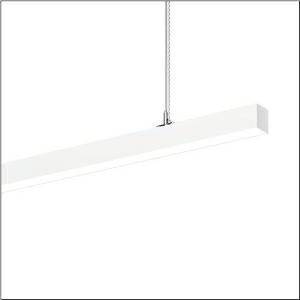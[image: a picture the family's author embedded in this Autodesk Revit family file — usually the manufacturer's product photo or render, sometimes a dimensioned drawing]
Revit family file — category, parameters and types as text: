
# Revit family: silica_r__21_51mx30tat4w_7b2a
name_source: partatom
category: Lighting Fixtures
units: mm (PartAtom-declared; Revit-internal decimal feet)

## family parameters
Cut with Voids When Loaded = No
Host = Face
Light Source = No
Part Type = Normal
Room Calculation Point = No
Round Connector Dimension = Use Diameter
Shared = No

## types (1)
- --- (1 x LED, 4120 lm, 33.8 W, 6500K)
    Apparent Load = 34 VA
    CIE Flux Codes = 47 79 96 58 100
    Color Rendering = 80
    Color Temperature = 6500K
    Default Elevation = 1800 mm
    Description = Silica® 21, office luminaire, primary optical cover: cover, of PMMA, opal, light emission: direct/indirect distribution, primary light characteristic: symmetric, installation type: suspended mounting, LED, rated luminous flux: 4.120lm, luminous efficacy: 116lm/W, light colour: 8tw, colour temperature: 2700..6500K, control gear: DALI DT8, with terminal, 3+2-pole, max. 2.5mm², mains connection: 220..240V, AC, 50/60Hz, rated input power: 35.5W, luminaire housing, of aluminium, traffic white (RAL 9016), length: 1.204mm, width: 53mm, height: 53mm, protection rating (complete): IP20, insulation class (complete): insulation class I (protective earthing), certification: CE, permissible operating ambient temperature: 0..+35°C, standard: EN 50419, packaging unit: 1 piece
    Height = 53 mm
    Lamp = 1 x LED
    Lamp Light Flux = 4120 lm
    Lamp Power = 33.8 W
    Lamp count = 1
    Length = 1204 mm
    Luminous efficacy = 122 lm/W
    Manufacturer = Siteco
    ModVariant = No
    Model = 51MX30TAT4W
    Mounting Place = Ceiling
    Mounting Type = Pendant
    Number of Poles = 1
    OnlyDefault = Yes
    Power Factor = 1
    Product Name = Silica® 21
    Product group = office luminaire | ceiling pendant
    ProductGroupID = 904
    Protection Class = Protection class I
    Protection Degree = IP 20
    RLX_Detail_Level = 1
    RLX_Emergency_Light_Flux = 0 lm
    RLX_Emergency_Type = 0
    RLX_Emergency_Type_DB = No
    RlxData = <blob elided: 17669 chars, md5=87303953>
    Socket = socket
    Standby Power = 0 W
    System Light Flux = 4120 lm
    System Power = 34 W
    Type Comments = individual setting
    Type Image = l_1349023.jpg
    URL = http://relux.com
    VarID = @adj_139656
    Voltage = 0 V
    Weight = 0.00 kg
    Width = 53 mm

## geometry (parser evidence)
native form markers: Blend x4, Sweep x12
no freeform markers — native parametric forms only
